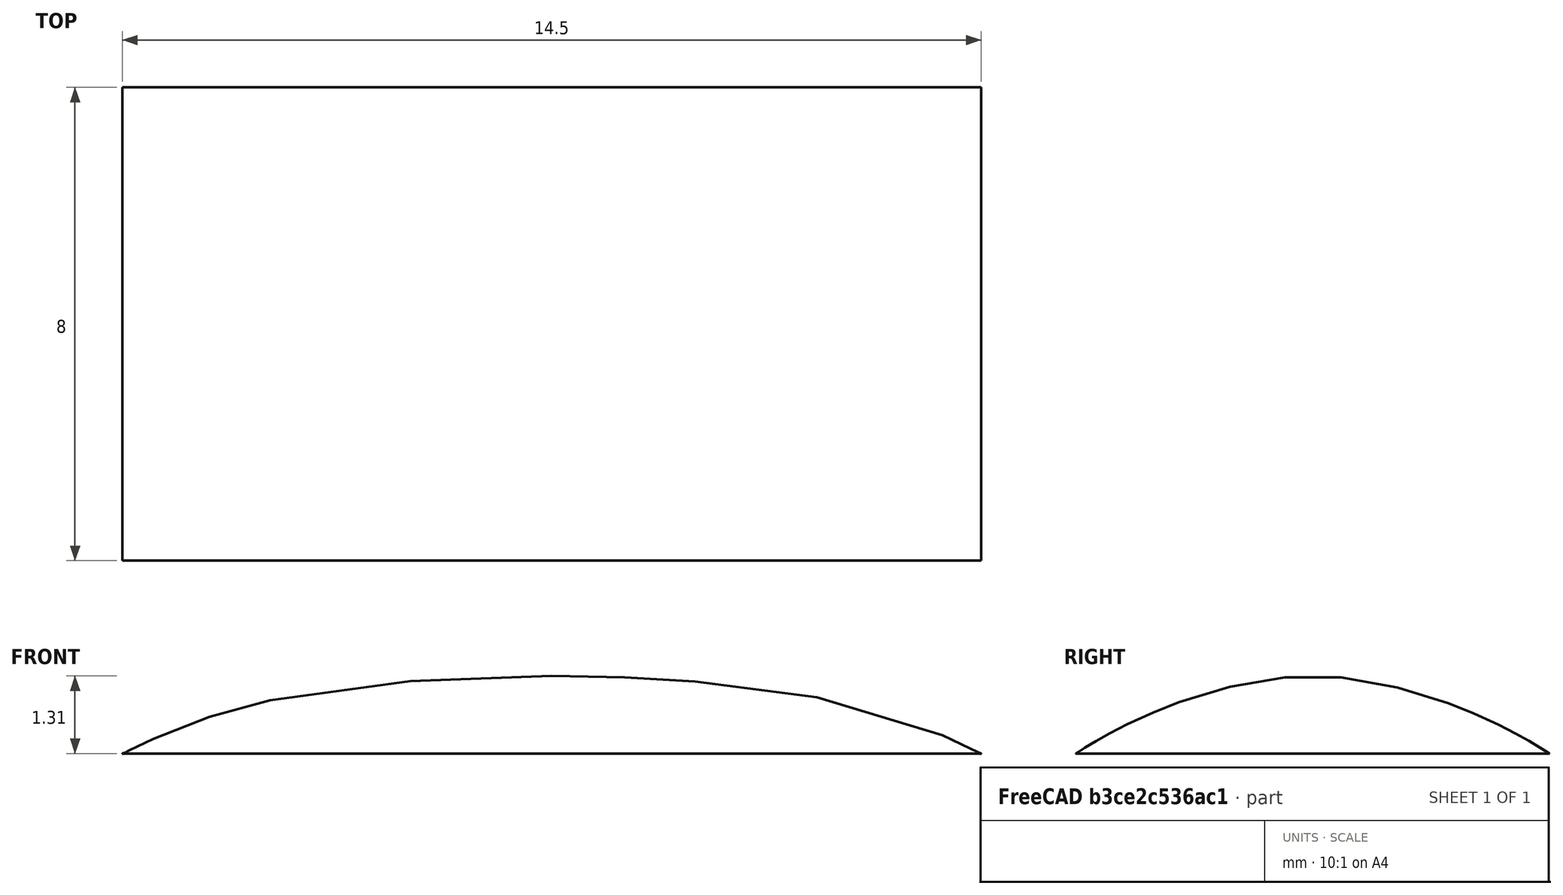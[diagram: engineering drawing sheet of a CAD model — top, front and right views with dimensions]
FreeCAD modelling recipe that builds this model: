
FCSTD DOCUMENT  (FreeCAD 0.20R29177 (Git))
Label: sensor_surface
License: All rights reserved
LicenseURL: http://en.wikipedia.org/wiki/All_rights_reserved
objects: Sketcher::SketchObject×3, Surface::Filling×1
note: 4 computed .brp shape members not serialized (recipe doc carries the construction recipe); baked Part::Feature solids carry a one-line shape summary decoded from their .brp

FEATURE [Sketcher::SketchObject] Sketch
  FullyConstrained = true
  sketch-geometry (4):
    g0: LineSegment StartX=0 StartY=0 StartZ=0 EndX=14.5 EndY=0 EndZ=0
    g1: LineSegment StartX=14.5 StartY=0 StartZ=0 EndX=14.5 EndY=-8 EndZ=0
    g2: LineSegment StartX=14.5 StartY=-8 StartZ=0 EndX=0 EndY=-8 EndZ=0
    g3: LineSegment StartX=0 StartY=-8 StartZ=0 EndX=0 EndY=0 EndZ=0
  constraints (11):
    c: Coincident(g0,g1)
    c: Coincident(g1,g2)
    c: Coincident(g2,g3)
    c: Coincident(g3,g0)
    c: Horizontal(g0)
    c: Horizontal(g2)
    c: Vertical(g1)
    c: Vertical(g3)
    c: Coincident(g0,g-1)
    c: DistanceX(g0,g0) = 14.5
    c: DistanceY(g1,g1) = 8
FEATURE [Sketcher::SketchObject] Sketch001
  ExternalGeometry = -> [Sketch]
  FullyConstrained = false
  Placement = pos=(0,-4,0) rot=(1,0,0;1.5708rad)
  sketch-geometry (7):
    g0-g3: Circle x4 (B-spline internal-alignment scaffolding for g4; pole/knot coordinates omitted)
    g4: BSplineCurve PolesCount=4 KnotsCount=2 Degree=3 IsPeriodic=0
    g5: GeomPoint X=0 Y=0 Z=0
    g6: GeomPoint X=14.5 Y=0 Z=0
  constraints (9):
    c: Weight(g0) = 1
    c: Coincident(g4,g-1)
    c: Equal(g0,g1)
    c: Equal(g0,g2)
    c: Equal(g0,g3)
    c: PointOnObject(g4,g-1)
    c: InternalAlignment(g0-g3 -> g4) x4
    c: InternalAlignment(g5,g4)
    c: InternalAlignment(g6,g4)
FEATURE [Sketcher::SketchObject] Sketch002
  ExternalGeometry = -> [Sketch,Sketch001]
  FullyConstrained = false
  Placement = pos=(7.25,0,0) rot=(0.57735,0.57735,0.57735;2.0944rad)
  sketch-geometry (6):
    g0: Circle CenterX=-7.99945 CenterY=0 CenterZ=0 NormalX=0 NormalY=0 NormalZ=1 AngleXU=0 Radius=1
    g1: Circle CenterX=-4.02191 CenterY=2.53433 CenterZ=0 NormalX=0 NormalY=0 NormalZ=1 AngleXU=0 Radius=1
    g2: Circle CenterX=0 CenterY=0 CenterZ=0 NormalX=0 NormalY=0 NormalZ=1 AngleXU=0 Radius=1
    g3: BSplineCurve PolesCount=3 KnotsCount=2 Degree=2 IsPeriodic=0
    g4: GeomPoint X=-7.99945 Y=0 Z=0
    g5: GeomPoint X=0 Y=0 Z=0
  constraints (10):
    c: Weight(g0) = 1
    c: PointOnObject(g3,g-1)
    c: Equal(g0,g1)
    c: Equal(g0,g2)
    c: Coincident(g3,g-1)
    c: InternalAlignment(g0,g3)
    c: InternalAlignment(g1,g3)
    c: InternalAlignment(g2,g3)
    c: InternalAlignment(g4,g3)
    c: InternalAlignment(g5,g3)
FEATURE [Surface::Filling] Surface
  Anisotropy = false
  BoundaryEdges = -> [Sketch]
  BoundaryOrder = [0,0,0,0]
  Degree = 3
  Iterations = 2
  MaximumDegree = 8
  MaximumSegments = 9
  PointsOnCurve = 15
  TolAngular = 0.01
  TolCurvature = 0.1
  Tolerance2d = 1e-05
  Tolerance3d = 0.0001
  UnboundEdges = -> [Sketch002,Sketch001]
  UnboundOrder = [0,0]
